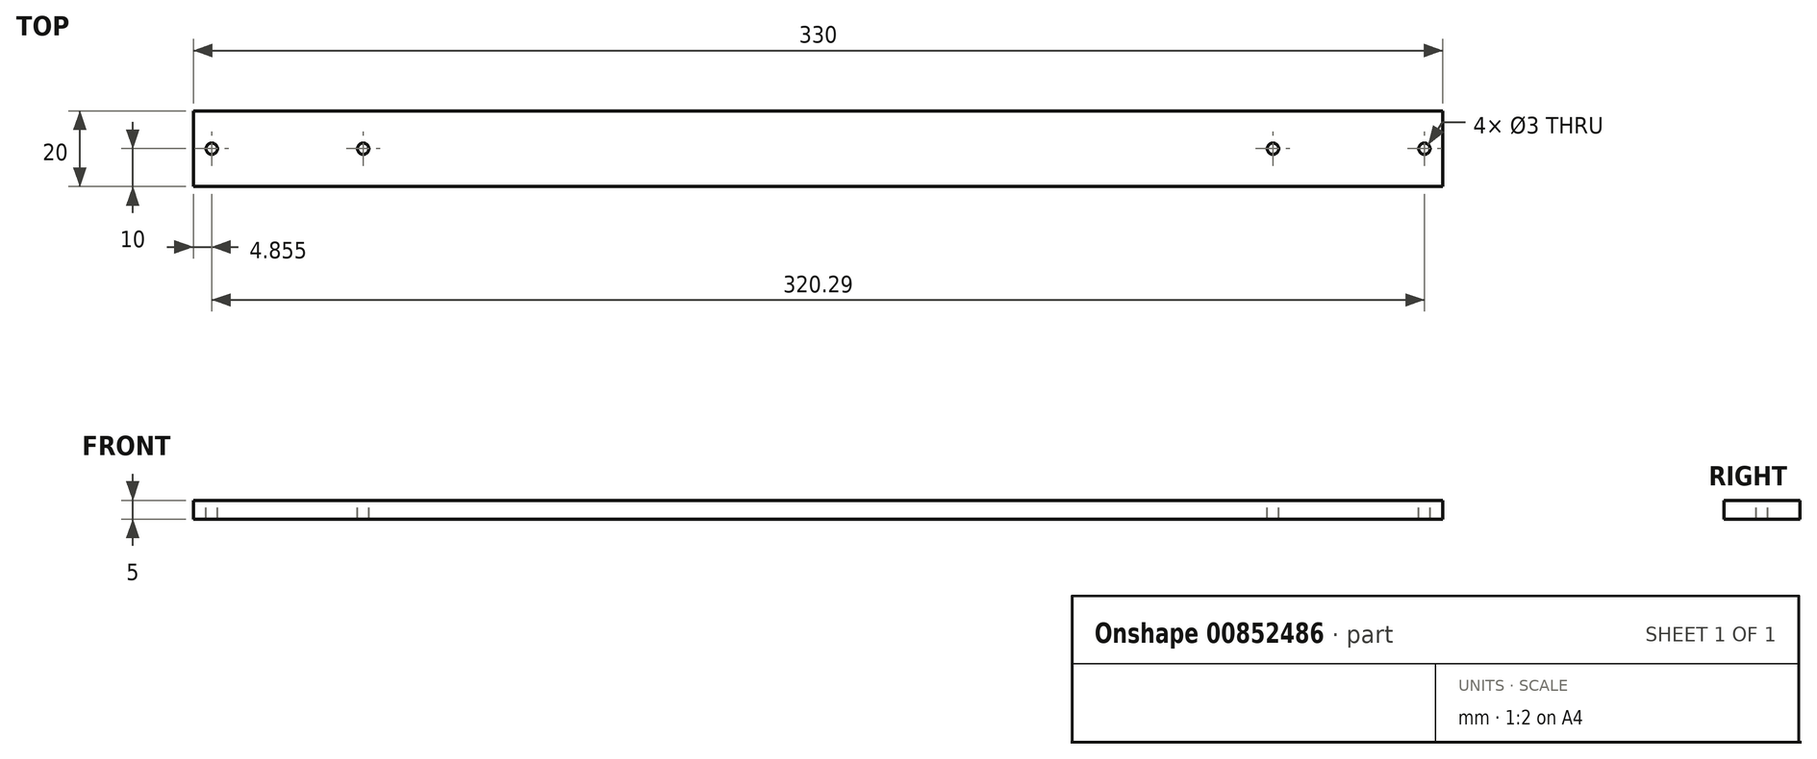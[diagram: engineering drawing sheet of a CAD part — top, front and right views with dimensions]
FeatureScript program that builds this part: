
annotation { "Feature Type Name" : "Feature", "Feature Type Description" : "" }
export const myFeature = defineFeature(function(context is Context, id is Id, definition is map)
    precondition{}
    {
        {
            var Q0;
            Q0=qCreatedBy(makeId("Top.planeOp"),FACE);
            var sketch = newSketch(context, id + "F0", { "sketchPlane" : qUnion([Q0])});
            skLineSegment(sketch, "E0.bottom", {"start": v(160.15, 0) * mm, "end": v(-160.15, 0) * mm});
            skLineSegment(sketch, "E0.top", {"start": v(160.15, 0) * mm, "end": v(-160.15, 0) * mm});
            skLineSegment(sketch, "E0.left", {"start": v(-160.14, 0) * mm, "end": v(-160.14, 0) * mm});
            skLineSegment(sketch, "E0.right", {"start": v(160.15, 0) * mm, "end": v(160.15, 0) * mm});
            skPoint(sketch, "E0.middle", {"position": v(0, 0) * mm});
            skLineSegment(sketch, "E1.bottom", {"start": v(165, -10) * mm, "end": v(-165, -10) * mm});
            skLineSegment(sketch, "E1.top", {"start": v(165, 10) * mm, "end": v(-165, 10) * mm});
            skLineSegment(sketch, "E1.left", {"start": v(165, -10) * mm, "end": v(165, 10) * mm});
            skLineSegment(sketch, "E1.right", {"start": v(-165, -10) * mm, "end": v(-165, 10) * mm});
            skPoint(sketch, "E2", {"position": v(-160.15, 0) * mm});
            skPoint(sketch, "E3", {"position": v(160.15, 0) * mm});
            skLineSegment(sketch, "E4.bottom", {"start": v(120.14, 0) * mm, "end": v(-120.14, 0) * mm});
            skLineSegment(sketch, "E4.top", {"start": v(120.14, 0) * mm, "end": v(-120.14, 0) * mm});
            skLineSegment(sketch, "E4.left", {"start": v(120.14, 0) * mm, "end": v(120.14, 0) * mm});
            skLineSegment(sketch, "E4.right", {"start": v(-120.14, 0) * mm, "end": v(-120.14, 0) * mm});
            skPoint(sketch, "E5", {"position": v(-120.14, 0) * mm});
            skPoint(sketch, "E6", {"position": v(120.14, 0) * mm});
            skSolve(sketch);
        }
        {
            var Q0;
            Q0=qSketchRegion(id+"F0",true);
            extrude(context, id + "F1", {"entities" : qUnion([Q0]), "oppositeDirection" : true, "depth" : 5 * mm, "offsetDistance" : 25 * mm});
        }
        {
            var Q0;
            Q0=sQuery(id+"F0.wireOp",VERTEX,"E2");
            var Q1;
            Q1=sQuery(id+"F0.wireOp",VERTEX,"E3");
            var Q2;
            Q2=makeQuery(id+"F1.opExtrude","SWEPT_BODY",BODY,{"disambiguationData":[OSD([sQuery(id+"F0.wireOp",EDGE,"E1.bottom"),sQuery(id+"F0.wireOp",EDGE,"E1.top"),sQuery(id+"F0.wireOp",EDGE,"E1.left"),sQuery(id+"F0.wireOp",EDGE,"E1.right")])]});
            hole(context, id + "F2", {"style" : HoleStyle.SIMPLE, "endStyle" : HoleEndStyle.THROUGH, "holeDiameter" : 3 * mm, "majorDiameter" : 5 * mm, "isTappedThrough" : true, "tappedDepth" : 12 * mm, "tapClearance" : 3, "locations" : qUnion([Q0, Q1]), "scope" : qUnion([Q2])});
        }
        {
            var Q0;
            Q0=sQuery(id+"F0.wireOp",VERTEX,"E5");
            var Q1;
            Q1=sQuery(id+"F0.wireOp",VERTEX,"E6");
            var Q2;
            Q2=makeQuery(id+"F1.opExtrude","SWEPT_BODY",BODY,{"disambiguationData":[OSD([sQuery(id+"F0.wireOp",EDGE,"E1.bottom"),sQuery(id+"F0.wireOp",EDGE,"E1.top"),sQuery(id+"F0.wireOp",EDGE,"E1.left"),sQuery(id+"F0.wireOp",EDGE,"E1.right")])]});
            hole(context, id + "F3", {"style" : HoleStyle.SIMPLE, "endStyle" : HoleEndStyle.THROUGH, "holeDiameter" : 3 * mm, "majorDiameter" : 5 * mm, "isTappedThrough" : true, "tappedDepth" : 12 * mm, "tapClearance" : 3, "locations" : qUnion([Q0, Q1]), "scope" : qUnion([Q2])});
        }
    });
